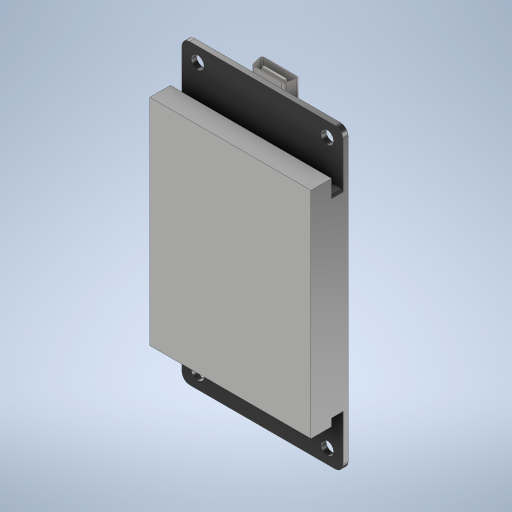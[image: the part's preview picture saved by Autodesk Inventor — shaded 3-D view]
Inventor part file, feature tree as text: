
AUTODESK INVENTOR PART (.ipt)
format: ipt  version: 2023 (Build 270158000, 158)  size: 456,192 bytes
history: native  units: mm
features: extrude x9, sketch x8, fillet x2, projected_geometry x2, other x1, mirror x1
ambient origin geometry x8: Origin, YZ Plane, XZ Plane, XY Plane, X Axis, Y Axis, Z Axis, Center Point
bodies: Body1 (feature_tree)
feature tree (23):
  other  "솔리드1"
  extrude  "돌출1"  Depth=31.2mm
  extrude  "돌출2"  Depth=57.6mm
  extrude  "돌출3"  Depth=2.5mm
  extrude  "돌출4"  Depth=25.1mm
  sketch  "스케치5"
  extrude  "돌출5"  Depth=1.0mm TaperAngle=0.0deg
  extrude  "돌출6"  Depth=1.5mm
  fillet  "모깎기1"  Radius=7.6mm
  extrude  "돌출7"  Depth=2.6mm
  extrude  "돌출8"  TaperAngle=15.0deg  [1 undecoded]
  mirror  "미러1"
  fillet  "모깎기2"  Radius=0.5mm
  extrude  "돌출12"  Depth=0.5mm
  sketch  "스케치1"
  sketch  "스케치2"
  sketch  "스케치3"
  projected_geometry  "투영된 루프1"
  sketch  "스케치4"
  projected_geometry  "투영된 루프2"
  sketch  "스케치6"
  sketch  "스케치7"
  sketch  "스케치10"
note: 1 required parameter value undecoded (feature->parameter linkage not recoverable at this tier; creation-order binding heuristic only, values carry confidence <= 0.55)
